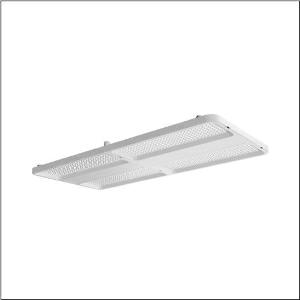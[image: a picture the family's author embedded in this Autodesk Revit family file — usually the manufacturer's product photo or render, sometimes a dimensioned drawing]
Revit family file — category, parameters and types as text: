
# Revit family: highbay_11_maxi_51hn12db4qba
name_source: partatom
category: Lighting Fixtures
units: mm (PartAtom-declared; Revit-internal decimal feet)

## family parameters
Cut with Voids When Loaded = No
Host = Face
Light Source = No
Part Type = Normal
Room Calculation Point = No
Round Connector Dimension = Use Diameter
Shared = No

## types (1)
- --- (1 x LED, 5620 lm, 27.8 W, 4000K)
    Apparent Load = 28 VA
    CIE Flux Codes = 87 98 100 100 100
    Color Rendering = 80
    Color Temperature = 4000K
    Default Elevation = 1800 mm
    Description = high bay luminaire Highbay 11 maxi; direct symmetric wide distribution, light control with lens of PMMA; UGR ≤ 22 (X = 4H | Y = 8H | S = 0.25H | reflection values 70/50/20); luminous flux: 36.000lm; light colour: 840, colour temperature: 4000K, MacAdam ≤ 2 SDCM (initial), colour rendering: CRI > 80; luminous efficacy: 202,6lm/W; rated service life: 100.000h (L95) at AT= 25°C; control: DALI 2; luminaire connection: terminal, 5-pole, max. 2.5mm² (cable entry for one cable, Ø 8.5..16mm); mains connection: 230..240V, AC/DC 0/50..60Hz; connected load: 177,7W; protection rating (complete): IP40; insulation class (complete): insulation class I (protective earthing); protection symbol: D; impact resistance: IK08; certification: CE, ENEC, VDE, UKCA; luminaire for central battery installations according to EN 60598-2-22, internal wiring halogen-free; luminaire corresponds to IFS (International Featured Standards) requirements for safety and quality in the food industry; LABS conformity tested according to VDMA 24364:2018-05; ball impact resistant only with use of appropriate mounting accessories; Suitable for use in the food industry according to the specifications of IFS-Food, HACCP and/or BRC; housing frame of high-performance plastic PA6, matt traffic white (RAL 9016); cover of PMMA; dimension (LxWxH): 946 x 442 x 72mm; permissible operating ambient temperature: -40..+55°C (reducing of maximum allowable ambient temperature of 5°C with ceiling mounting); packaging unit: 1 piece; (delivery without accessories; please order mounting accessories separately)
    Height = 72 mm  [stored 0.23622 ft]
    Lamp = 1 x LED
    Lamp Light Flux = 5620 lm
    Lamp Power = 27.8 W
    Lamp count = 1
    Length = 946 mm
    Luminous efficacy = 202 lm/W
    Manufacturer = Siteco
    ModVariant = No
    Model = 51HN12DB4QBA
    Mounting Place = Ceiling
    Mounting Type = Pendant
    Number of Poles = 1
    OnlyDefault = Yes
    Power Factor = 1
    Product Name = Highbay 11 maxi
    Product group = high bay luminaire
    ProductGroupID = 902
    Protection Class = Protection class I
    Protection Degree = IP 40
    RLX_Detail_Level = 1
    RLX_Emergency_Light_Flux = 0 lm
    RLX_Emergency_Type = 0
    RLX_Emergency_Type_DB = No
    RlxData = <blob elided: 127773 chars, md5=2a8abc4c>
    Socket = socket
    Standby Power = 0 W
    System Light Flux = 5620 lm
    System Power = 28 W
    Type Comments = : DC mode (central or group accumulator) initial emergency light level
    Type Image = l_1376023.jpg
    URL = http://relux.com
    VarID = @adj_016323
    Voltage = 0 V
    Weight = 0.00 kg
    Width = 442 mm

note: [stored X ft] marks values corroborated as IEEE doubles in the binary element streams (Revit-internal decimal feet)

## geometry (parser evidence)
native form markers: Blend x4, Sweep x10
no freeform markers — native parametric forms only
